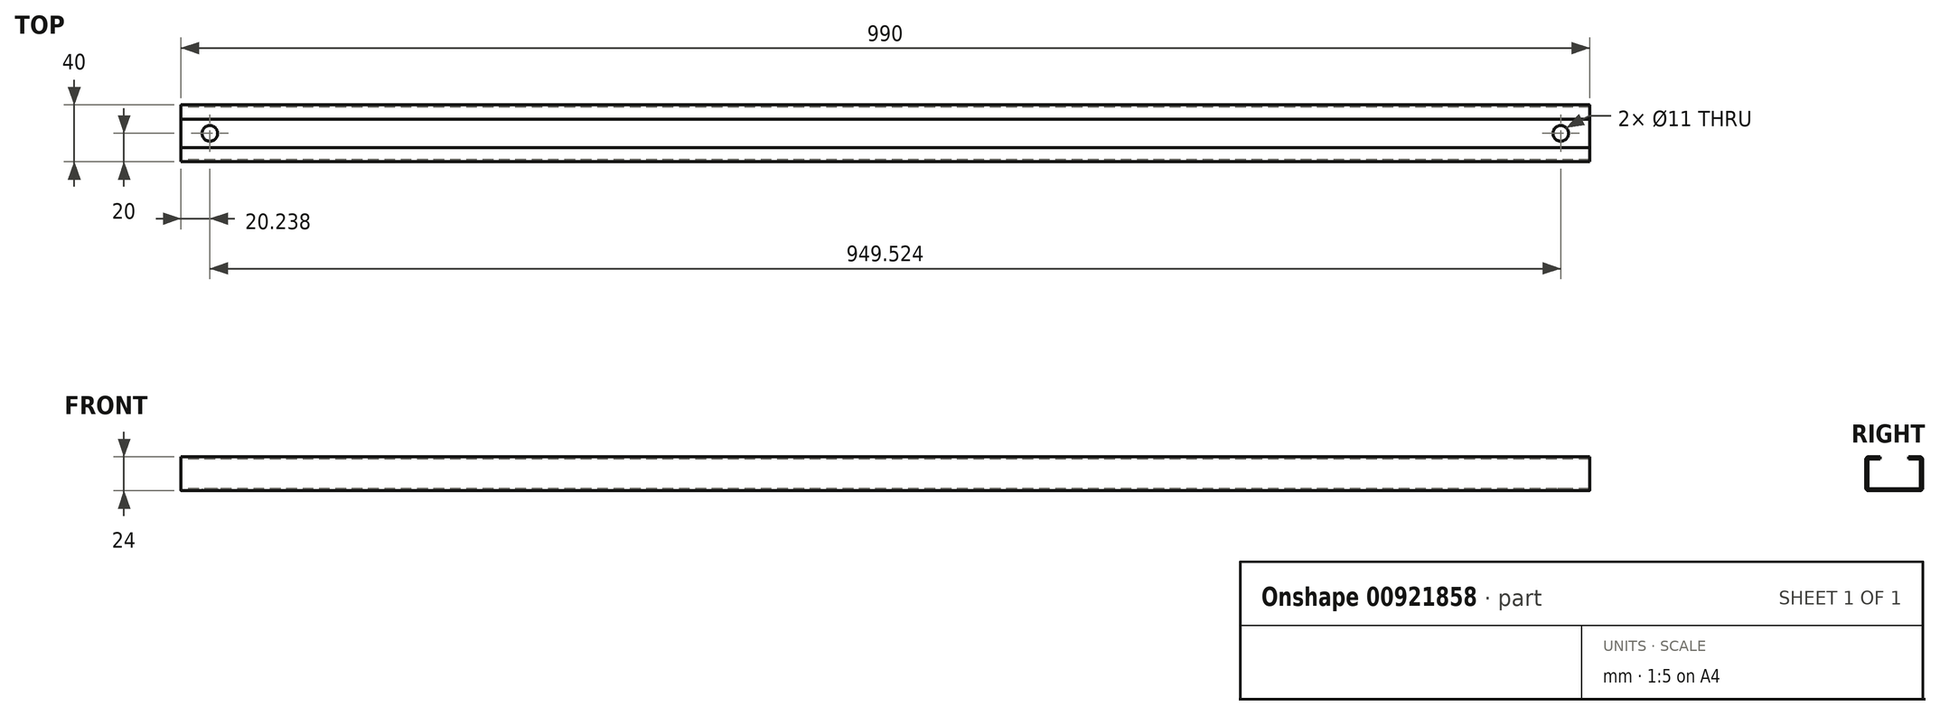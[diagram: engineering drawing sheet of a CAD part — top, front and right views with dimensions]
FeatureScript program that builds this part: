
annotation { "Feature Type Name" : "Feature", "Feature Type Description" : "" }
export const myFeature = defineFeature(function(context is Context, id is Id, definition is map)
    precondition{}
    {
        {
            var Q0;
            Q0=qCreatedBy(makeId("Right.planeOp"),FACE);
            var sketch = newSketch(context, id + "F0", { "sketchPlane" : qUnion([Q0])});
            skLineSegment(sketch, "E0.top", {"start": v(-59.93, 5.94) * mm, "end": v(-23.93, 5.94) * mm});
            skLineSegment(sketch, "E0.left", {"start": v(-61.93, 27.94) * mm, "end": v(-61.93, 7.94) * mm});
            skLineSegment(sketch, "E0.right", {"start": v(-21.93, 27.94) * mm, "end": v(-21.93, 7.94) * mm});
            skLineSegment(sketch, "E1.1", {"start": v(-60.43, 27.44) * mm, "end": v(-60.43, 8.44) * mm});
            skLineSegment(sketch, "E1.2", {"start": v(-59.43, 7.44) * mm, "end": v(-24.43, 7.44) * mm});
            skLineSegment(sketch, "E1.3", {"start": v(-23.43, 27.44) * mm, "end": v(-23.43, 8.44) * mm});
            skLineSegment(sketch, "E2", {"start": v(-23.93, 29.94) * mm, "end": v(-31.93, 29.94) * mm});
            skLineSegment(sketch, "E3", {"start": v(-31.93, 29.94) * mm, "end": v(-31.93, 28.44) * mm});
            skLineSegment(sketch, "E4", {"start": v(-31.93, 28.44) * mm, "end": v(-24.43, 28.44) * mm});
            skLineSegment(sketch, "E5", {"start": v(-59.93, 29.94) * mm, "end": v(-51.93, 29.94) * mm});
            skLineSegment(sketch, "E6", {"start": v(-51.93, 29.94) * mm, "end": v(-51.93, 28.44) * mm});
            skLineSegment(sketch, "E7", {"start": v(-51.93, 28.44) * mm, "end": v(-59.43, 28.44) * mm});
            skPoint(sketch, "E8.visualSharp", {"position": v(-61.93, 29.94) * mm});
            skArc(sketch, "E8.filletArc", {"start": v(-59.93, 29.94) * mm, "mid": v(-61.34, 29.35) * mm, "end": v(-61.93, 27.94) * mm});
            skPoint(sketch, "E9.visualSharp", {"position": v(-61.93, 5.94) * mm});
            skArc(sketch, "E9.filletArc", {"start": v(-61.93, 7.94) * mm, "mid": v(-61.34, 6.52) * mm, "end": v(-59.93, 5.94) * mm});
            skPoint(sketch, "E10.visualSharp", {"position": v(-21.93, 5.94) * mm});
            skArc(sketch, "E10.filletArc", {"start": v(-23.93, 5.94) * mm, "mid": v(-22.52, 6.52) * mm, "end": v(-21.93, 7.94) * mm});
            skPoint(sketch, "E11.visualSharp", {"position": v(-21.93, 29.94) * mm});
            skArc(sketch, "E11.filletArc", {"start": v(-21.93, 27.94) * mm, "mid": v(-22.52, 29.35) * mm, "end": v(-23.93, 29.94) * mm});
            skPoint(sketch, "E12.visualSharp", {"position": v(-23.43, 28.44) * mm});
            skArc(sketch, "E12.filletArc", {"start": v(-23.43, 27.44) * mm, "mid": v(-23.72, 28.15) * mm, "end": v(-24.43, 28.44) * mm});
            skPoint(sketch, "E13.visualSharp", {"position": v(-23.43, 7.44) * mm});
            skArc(sketch, "E13.filletArc", {"start": v(-24.43, 7.44) * mm, "mid": v(-23.72, 7.73) * mm, "end": v(-23.43, 8.44) * mm});
            skPoint(sketch, "E14.visualSharp", {"position": v(-60.43, 7.44) * mm});
            skArc(sketch, "E14.filletArc", {"start": v(-60.43, 8.44) * mm, "mid": v(-60.14, 7.73) * mm, "end": v(-59.43, 7.44) * mm});
            skPoint(sketch, "E15.visualSharp", {"position": v(-60.43, 28.44) * mm});
            skArc(sketch, "E15.filletArc", {"start": v(-59.43, 28.44) * mm, "mid": v(-60.14, 28.15) * mm, "end": v(-60.43, 27.44) * mm});
            skSolve(sketch);
        }
        {
            var Q0;
            Q0=makeQuery(id+"F0.imprint","IMPRINT",FACE,{"disambiguationData":[TD([[makeQuery(id+"F0.imprint","IMPRINT",EDGE,{"derivedFrom":sQuery(id+"F0.wireOp",EDGE,"E0.top")}),1.0]])]});
            extrude(context, id + "F1", {"entities" : qUnion([Q0]), "depth" : 990 * mm, "offsetDistance" : 25 * mm});
        }
        {
            var Q0;
            Q0=makeQuery(id+"F1.opExtrude","SWEPT_FACE",FACE,{"disambiguationData":[OSD([sQuery(id+"F0.wireOp",EDGE,"E0.top")])]});
            var sketch = newSketch(context, id + "F2", { "sketchPlane" : qUnion([Q0])});
            skLineSegment(sketch, "E16", {"start": v(0, 41.93) * mm, "end": v(20.24, 41.93) * mm});
            skLineSegment(sketch, "E17", {"start": v(990, 41.93) * mm, "end": v(969.76, 41.93) * mm});
            skSolve(sketch);
        }
        {
            var Q0;
            Q0=sQuery(id+"F2.wireOp",VERTEX,"E17.end");
            var Q1;
            Q1=sQuery(id+"F2.wireOp",VERTEX,"E16.end");
            var Q2;
            Q2=makeQuery(id+"F1.opExtrude","SWEPT_BODY",BODY,{"disambiguationData":[OSD([sQuery(id+"F0.wireOp",EDGE,"E0.top"),sQuery(id+"F0.wireOp",EDGE,"E0.left"),sQuery(id+"F0.wireOp",EDGE,"E0.right"),sQuery(id+"F0.wireOp",EDGE,"E1.1"),sQuery(id+"F0.wireOp",EDGE,"E1.2"),sQuery(id+"F0.wireOp",EDGE,"E1.3"),sQuery(id+"F0.wireOp",EDGE,"E2"),sQuery(id+"F0.wireOp",EDGE,"E3"),sQuery(id+"F0.wireOp",EDGE,"E4"),sQuery(id+"F0.wireOp",EDGE,"E5"),sQuery(id+"F0.wireOp",EDGE,"E6"),sQuery(id+"F0.wireOp",EDGE,"E7"),sQuery(id+"F0.wireOp",EDGE,"E8.filletArc"),sQuery(id+"F0.wireOp",EDGE,"E9.filletArc"),sQuery(id+"F0.wireOp",EDGE,"E10.filletArc"),sQuery(id+"F0.wireOp",EDGE,"E11.filletArc"),sQuery(id+"F0.wireOp",EDGE,"E12.filletArc"),sQuery(id+"F0.wireOp",EDGE,"E13.filletArc"),sQuery(id+"F0.wireOp",EDGE,"E14.filletArc"),sQuery(id+"F0.wireOp",EDGE,"E15.filletArc")])]});
            hole(context, id + "F3", {"style" : HoleStyle.SIMPLE, "endStyle" : HoleEndStyle.THROUGH, "holeDiameter" : 11 * mm, "majorDiameter" : 5 * mm, "isTappedThrough" : true, "tappedDepth" : 12 * mm, "tapClearance" : 3, "locations" : qUnion([Q0, Q1]), "scope" : qUnion([Q2])});
        }
    });
